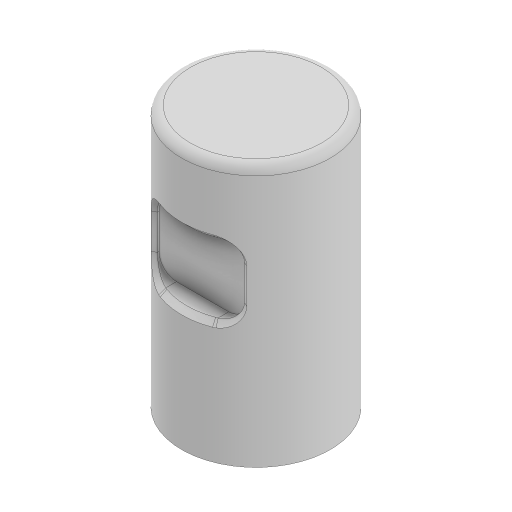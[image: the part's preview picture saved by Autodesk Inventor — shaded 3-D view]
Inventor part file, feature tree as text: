
AUTODESK INVENTOR PART (.ipt)
format: ipt  version: 2023 (Build 270158000, 158)  size: 165,888 bytes
history: native  units: mm
features: sketch x3, other x2, extrude x2, fillet x1, chamfer x1
ambient origin geometry x8: Origin, YZ Plane, XZ Plane, XY Plane, X Axis, Y Axis, Z Axis, Center Point
bodies: Body1 (feature_tree)
feature tree (9):
  other  "ソリッド1"
  extrude  "押し出し1"  Depth=85.3mm
  fillet  "フィレット1"  Radius=149.86mm
  sketch  "スケッチ2"
  other  "作業平面1"
  extrude  "押し出し2"  Depth=5.0mm
  chamfer  "面取り1"  Distance=90.0mm
  sketch  "スケッチ1"
  sketch  "スケッチ3"
